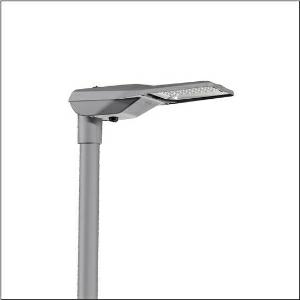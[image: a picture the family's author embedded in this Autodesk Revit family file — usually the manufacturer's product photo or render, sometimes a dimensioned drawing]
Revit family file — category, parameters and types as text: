
# Revit family: streetlight_sl_21_mini___st1_5a_5xe2p43t08gb_00fd
name_source: partatom
category: Lighting Fixtures
units: mm (PartAtom-declared; Revit-internal decimal feet)

## family parameters
Cut with Voids When Loaded = No
Host = Face
Light Source = No
Part Type = Normal
Room Calculation Point = No
Round Connector Dimension = Use Diameter
Shared = No

## types (1)
- --- (1 x LED, 6080 lm, 40.4 W, 4000K)
    Apparent Load = 40 VA
    CIE Flux Codes = 22 53 95 100 100
    Color Rendering = 70
    Color Temperature = 4000K
    Default Elevation = 1800 mm
    Description = Streetlight SL 21 mini, mast luminaire, primary light control with lens, of PMMA, primary optical cover: cover, of toughened safety glass, transparent, light distribution: ST1.5a, light emission: direct distribution, primary light characteristic: asymmetric, installation type: side-entry, post-top, LED, High Power LED, rated luminous flux: 6.080lm, luminous efficacy: 151lm/W, light colour: 740, colour temperature: 4000K, control gear: D4i, control: overheat protection, constant luminous flux control, time-dependent luminous flux control, flexible luminous flux parameterisation, pre-setting: logarithmic dimming characteristic, mains connection: 220..240V, AC, 50/60Hz, start of lifetime: 40W, end of service life: 41W, reduction: 19W, luminaire housing, of diecast aluminium, powder-coated, SITECO metallic grey (DB 702S), corrosivity category C5 high according to DIN EN ISO 12944, please order mast flange separately, inclination adjustable: 0°, 5°, 10°, 15°, sealing non-destructively replaceable, multi-level sealing system, length: 628mm, width: 235mm, height: 110mm, mast flange for spigot size: 42mm (side-entry): 5XC10008XM4, 60/48mm (side-entry/post-top): 5XC10108XM2, 76/60mm (side-entry/post-top): 5XC10108XM1, mounting height: 4..8m, Smart Interface below and above, protection rating (complete): IP66, insulation class (complete): insulation class II (safety insulation), certification: CE, ENEC, ENEC+, VDE, impact resistance: IK10, permissible operating ambient temperature for outdoor applications: -40..+50°C, standard-compliant lighting for roads and squares, packaging unit: 1 piece

Light Distribution: ST1.5a
    Height = 110 mm
    Lamp = 1 x LED
    Lamp Light Flux = 6080 lm
    Lamp Power = 40.4 W
    Lamp count = 1
    Length = 625 mm
    Luminous efficacy = 151 lm/W
    Manufacturer = Siteco
    ModVariant = No
    Model = 5XE2P43T08GB
    Number of Poles = 1
    OnlyDefault = Yes
    Power Factor = 1
    Product Name = Streetlight SL 21 mini | ST1.5a
    Product group = mast luminaire | pylon top
    ProductGroupID = 6100
    Protection Class = Protection class II
    Protection Degree = IP 66
    RLX_Detail_Level = 1
    RLX_Emergency_Light_Flux = 0 lm
    RLX_Emergency_Type = 0
    RLX_Emergency_Type_DB = No
    RlxData = <blob elided: 29817 chars, md5=7c3339fa>
    Socket = socket
    Standby Power = 0 W
    System Light Flux = 6080 lm
    System Power = 40 W
    Type Comments = factory setting: luminous flux: 100 % | dim-lin: 254 | 812 mA
    Type Image = l_1003514.jpg
    URL = http://relux.com
    VarID = @adj_175013
    Voltage = 0 V
    Weight = 0.00 kg
    Width = 234 mm

## geometry (parser evidence)
native form markers: Blend x4, Sweep x9
no freeform markers — native parametric forms only
